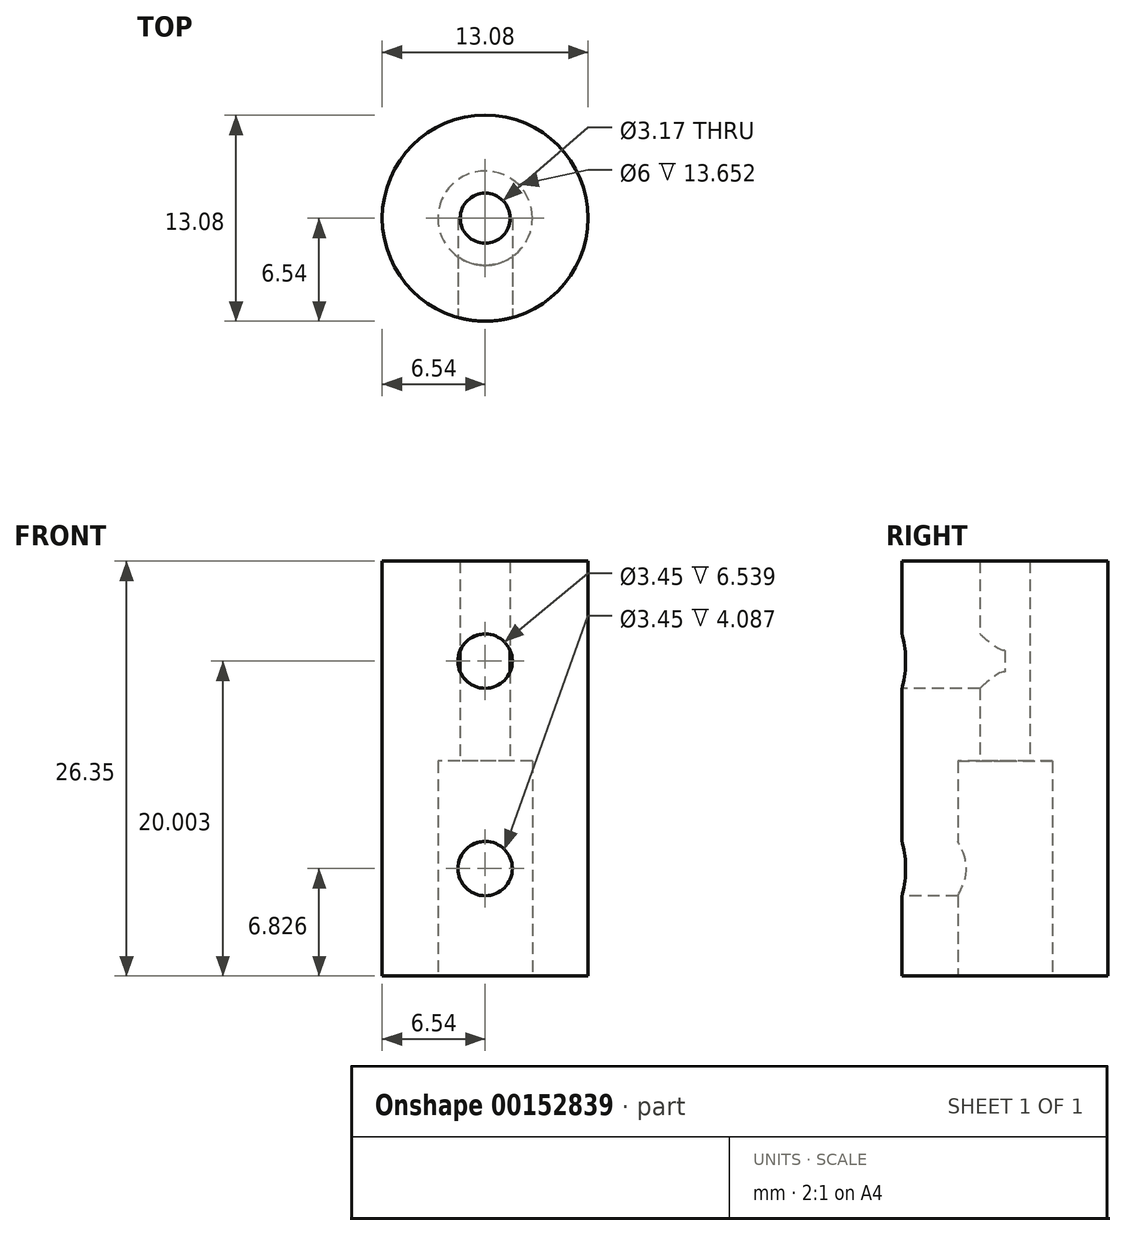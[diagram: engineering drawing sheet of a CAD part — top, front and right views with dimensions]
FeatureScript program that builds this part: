
annotation { "Feature Type Name" : "Feature", "Feature Type Description" : "" }
export const myFeature = defineFeature(function(context is Context, id is Id, definition is map)
    precondition{}
    {
        {
            var Q0;
            Q0=qCreatedBy(makeId("Top.planeOp"),FACE);
            var sketch = newSketch(context, id + "F0", { "sketchPlane" : qUnion([Q0])});
            skCircle(sketch, "E0", {"center": v(0, 0) * mm, "radius": 3 * mm});
            skCircle(sketch, "E1", {"center": v(0, 0) * mm, "radius": 6.54 * mm, "construction": true});
            skLineSegment(sketch, "E2.bottom", {"start": v(6.54, 6.54) * mm, "end": v(-6.54, 6.54) * mm});
            skLineSegment(sketch, "E2.top", {"start": v(6.54, -6.54) * mm, "end": v(-6.54, -6.54) * mm});
            skLineSegment(sketch, "E2.left", {"start": v(6.54, 6.54) * mm, "end": v(6.54, -6.54) * mm});
            skLineSegment(sketch, "E2.right", {"start": v(-6.54, 6.54) * mm, "end": v(-6.54, -6.54) * mm});
            skLineSegment(sketch, "E3", {"start": v(0, 0) * mm, "end": v(3, 0) * mm, "construction": true});
            skLineSegment(sketch, "E4.bottom", {"start": v(3, 2.15) * mm, "end": v(6.17, 2.15) * mm, "construction": true});
            skLineSegment(sketch, "E4.top", {"start": v(3, -2.15) * mm, "end": v(6.17, -2.15) * mm, "construction": true});
            skLineSegment(sketch, "E4.left", {"start": v(3, 2.15) * mm, "end": v(3, -2.15) * mm, "construction": true});
            skLineSegment(sketch, "E4.right", {"start": v(6.17, 2.15) * mm, "end": v(6.17, -2.15) * mm, "construction": true});
            skSolve(sketch);
        }
        {
            var Q0;
            Q0=qSketchRegion(id+"F0",true);
            extrude(context, id + "F1", {"entities" : qUnion([Q0]), "depth" : 13.65 * mm});
        }
        {
            var Q0;
            Q0=makeQuery(id+"F1.opExtrude","CAP_FACE",FACE,{"disambiguationData":[OSD([sQuery(id+"F0.wireOp",EDGE,"E0"),sQuery(id+"F0.wireOp",EDGE,"E2.bottom"),sQuery(id+"F0.wireOp",EDGE,"E2.top"),sQuery(id+"F0.wireOp",EDGE,"E2.left"),sQuery(id+"F0.wireOp",EDGE,"E2.right")])],"isStart":false});
            var sketch = newSketch(context, id + "F2", { "sketchPlane" : qUnion([Q0])});
            skCircle(sketch, "E5", {"center": v(0, 0) * mm, "radius": 1.59 * mm});
            skLineSegment(sketch, "E6.bottom", {"start": v(6.54, 6.54) * mm, "end": v(-6.54, 6.54) * mm});
            skLineSegment(sketch, "E6.top", {"start": v(6.54, -6.54) * mm, "end": v(-6.54, -6.54) * mm});
            skLineSegment(sketch, "E6.left", {"start": v(6.54, 6.54) * mm, "end": v(6.54, -6.54) * mm});
            skLineSegment(sketch, "E6.right", {"start": v(-6.54, 6.54) * mm, "end": v(-6.54, -6.54) * mm});
            skSolve(sketch);
        }
        {
            var Q0;
            Q0=qSketchRegion(id+"F2",true);
            extrude(context, id + "F3", {"entities" : qUnion([Q0]), "operationType" : NewBodyOperationType.ADD, "depth" : 12.7 * mm});
        }
        {
            var Q0;
            Q0=makeQuery(id+"F3.boolean.opBoolean","MERGE",FACE,{"derivedFrom":[makeQuery(id+"F1.opExtrude","SWEPT_FACE",FACE,{"disambiguationData":[OSD([sQuery(id+"F0.wireOp",EDGE,"E2.top")])]}),makeQuery(id+"F3.opExtrude","SWEPT_FACE",FACE,{"disambiguationData":[OSD([sQuery(id+"F2.wireOp",EDGE,"E6.top")])]})]});
            var sketch = newSketch(context, id + "F4", { "sketchPlane" : qUnion([Q0])});
            skLineSegment(sketch, "E7", {"start": v(0, 26.35) * mm, "end": v(0, 13.65) * mm, "construction": true});
            skLineSegment(sketch, "E8", {"start": v(0, 13.65) * mm, "end": v(0, 0) * mm, "construction": true});
            skCircle(sketch, "E9", {"center": v(0, 20) * mm, "radius": 1.73 * mm});
            skCircle(sketch, "E10", {"center": v(0, 6.83) * mm, "radius": 1.73 * mm});
            skSolve(sketch);
        }
        {
            var Q0;
            Q0=qSketchRegion(id+"F4",true);
            extrude(context, id + "F5", {"entities" : qUnion([Q0]), "operationType" : NewBodyOperationType.REMOVE, "oppositeDirection" : true, "depth" : 6.54 * mm});
        }
        {
            var Q0;
            Q0=makeQuery(id+"F1.opExtrude","SWEPT_EDGE",EDGE,{"disambiguationData":[OSD([sQuery(id+"F0.wireOp",EDGE,"E2.top"),sQuery(id+"F0.wireOp",EDGE,"E2.right")])]});
            var Q1;
            Q1=makeQuery(id+"F1.opExtrude","SWEPT_EDGE",EDGE,{"disambiguationData":[OSD([sQuery(id+"F0.wireOp",EDGE,"E2.bottom"),sQuery(id+"F0.wireOp",EDGE,"E2.right")])]});
            var Q2;
            Q2=makeQuery(id+"F1.opExtrude","SWEPT_EDGE",EDGE,{"disambiguationData":[OSD([sQuery(id+"F0.wireOp",EDGE,"E2.top"),sQuery(id+"F0.wireOp",EDGE,"E2.left")])]});
            var Q3;
            Q3=makeQuery(id+"F1.opExtrude","SWEPT_EDGE",EDGE,{"disambiguationData":[OSD([sQuery(id+"F0.wireOp",EDGE,"E2.bottom"),sQuery(id+"F0.wireOp",EDGE,"E2.left")])]});
            fillet(context, id + "F6", {"entities" : qUnion([Q0, Q1, Q2, Q3]), "radius" : 6.54 * mm, "tangentPropagation" : true, "allowEdgeOverflow" : false});
        }
    });
